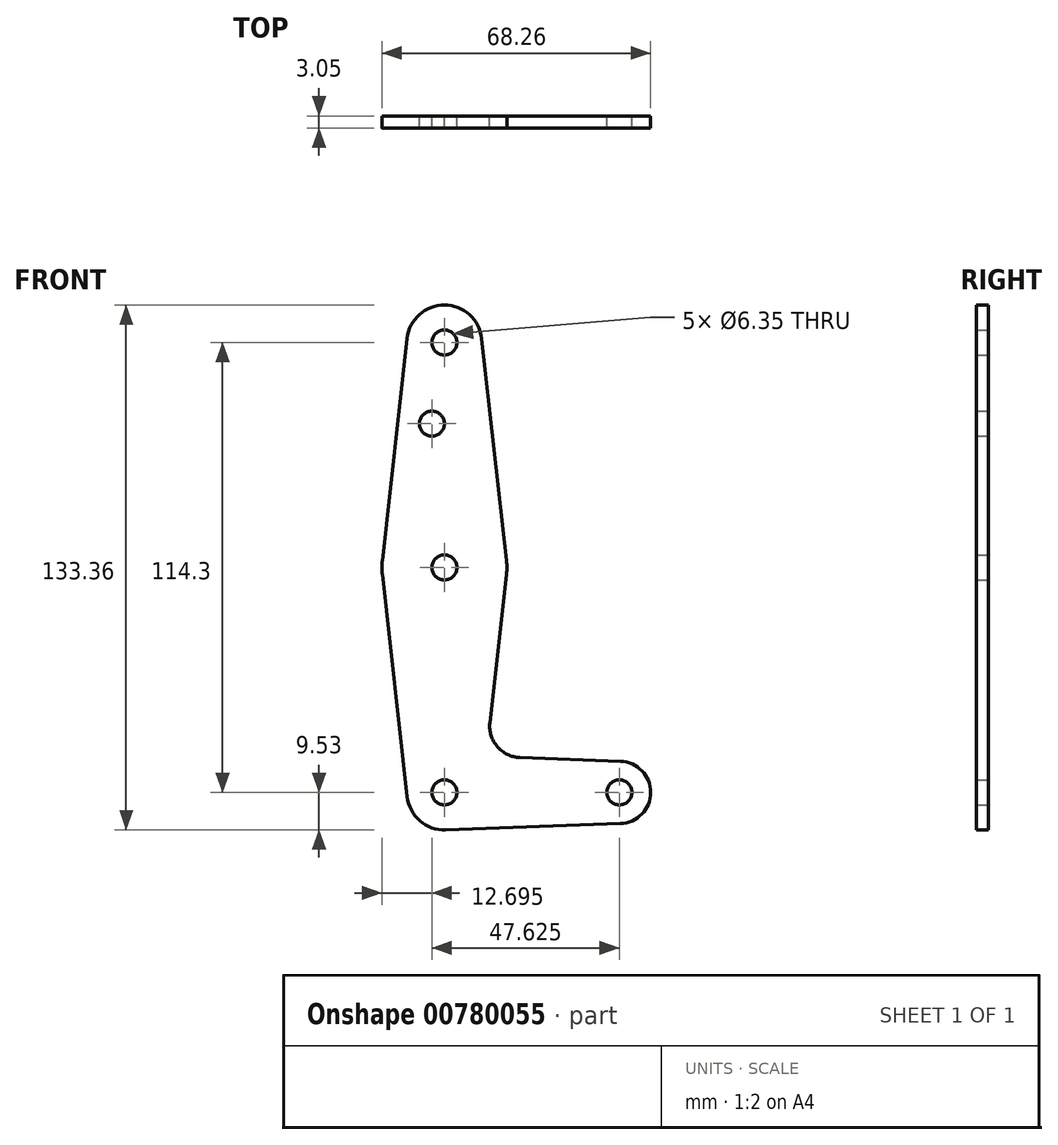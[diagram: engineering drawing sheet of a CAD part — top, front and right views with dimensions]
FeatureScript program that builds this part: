
annotation { "Feature Type Name" : "Feature", "Feature Type Description" : "" }
export const myFeature = defineFeature(function(context is Context, id is Id, definition is map)
    precondition{}
    {
        {
            var Q0;
            Q0=qCreatedBy(makeId("Front.planeOp"),FACE);
            var sketch = newSketch(context, id + "F0", { "sketchPlane" : qUnion([Q0])});
            skLineSegment(sketch, "E0", {"start": v(44.45, 0) * mm, "end": v(0, 0) * mm, "construction": true});
            skLineSegment(sketch, "E1", {"start": v(0, 0) * mm, "end": v(0, 114.3) * mm, "construction": true});
            skCircle(sketch, "E2", {"center": v(0, 114.3) * mm, "radius": 9.53 * mm});
            skCircle(sketch, "E3", {"center": v(44.45, 0) * mm, "radius": 7.94 * mm});
            skCircle(sketch, "E4", {"center": v(0, 0) * mm, "radius": 9.53 * mm});
            skCircle(sketch, "E5", {"center": v(0, 57.15) * mm, "radius": 15.88 * mm});
            skLineSegment(sketch, "E6", {"start": v(9.47, 115.36) * mm, "end": v(15.78, 58.91) * mm});
            skLineSegment(sketch, "E7", {"start": v(-9.47, 115.36) * mm, "end": v(-15.78, 58.91) * mm});
            skLineSegment(sketch, "E8", {"start": v(-15.78, 55.39) * mm, "end": v(-9.47, -1.06) * mm});
            skLineSegment(sketch, "E9", {"start": v(15.78, 55.39) * mm, "end": v(11.56, 17.67) * mm});
            skLineSegment(sketch, "E10", {"start": v(19.18, 8.85) * mm, "end": v(44.73, 7.93) * mm});
            skLineSegment(sketch, "E11", {"start": v(0.34, -9.52) * mm, "end": v(44.73, -7.93) * mm});
            skCircle(sketch, "E12", {"center": v(0, 114.3) * mm, "radius": 3.18 * mm});
            skCircle(sketch, "E13", {"center": v(-3.18, 93.68) * mm, "radius": 3.18 * mm});
            skCircle(sketch, "E14", {"center": v(0, 57.15) * mm, "radius": 3.18 * mm});
            skCircle(sketch, "E15", {"center": v(0, 0) * mm, "radius": 3.18 * mm});
            skCircle(sketch, "E16", {"center": v(44.45, 0) * mm, "radius": 3.18 * mm});
            skArc(sketch, "E17.filletArc", {"start": v(11.56, 17.67) * mm, "mid": v(13.44, 11.6) * mm, "end": v(19.18, 8.85) * mm});
            skSolve(sketch);
        }
        {
            var Q0;
            Q0 = qSketchRegion(id + "F0", true);
            extrude(context, id + "F1", {"entities" : qUnion([Q0]), "depth" : 3.05 * mm, "offsetDistance" : 25.4 * mm});
        }
    });
